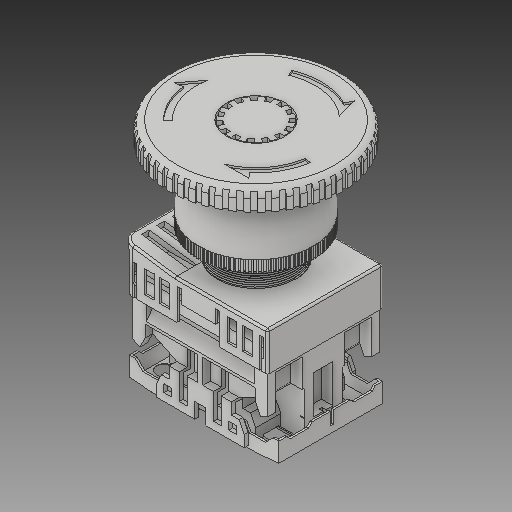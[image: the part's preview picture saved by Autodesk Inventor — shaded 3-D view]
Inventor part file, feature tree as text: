
AUTODESK INVENTOR PART (.ipt)
format: ipt  version: 2017 (Build 210142000, 142)  size: 1,958,400 bytes
history: native  units: mm
features: fillet x2, other x2, mirror x2
ambient origin geometry x8: Origin, YZ Plane, XZ Plane, XY Plane, X Axis, Y Axis, Z Axis, Center Point
bodies: Solid1 (feature_tree), Solid2 (feature_tree), Solid3 (feature_tree), Solid4 (feature_tree), Solid5 (feature_tree), Solid6 (feature_tree)
feature tree (6):
  fillet  "Fillet4"  [1 undecoded]
  fillet  "Fillet3"  [1 undecoded]
  other  "Cut-Extrude21[1]"
  mirror  "Mirror22[1]"
  mirror  "Mirror22[2]"
  other  "Cut-Extrude25"
note: 2 required parameter values undecoded (feature->parameter linkage not recoverable at this tier; creation-order binding heuristic only, values carry confidence <= 0.55)
